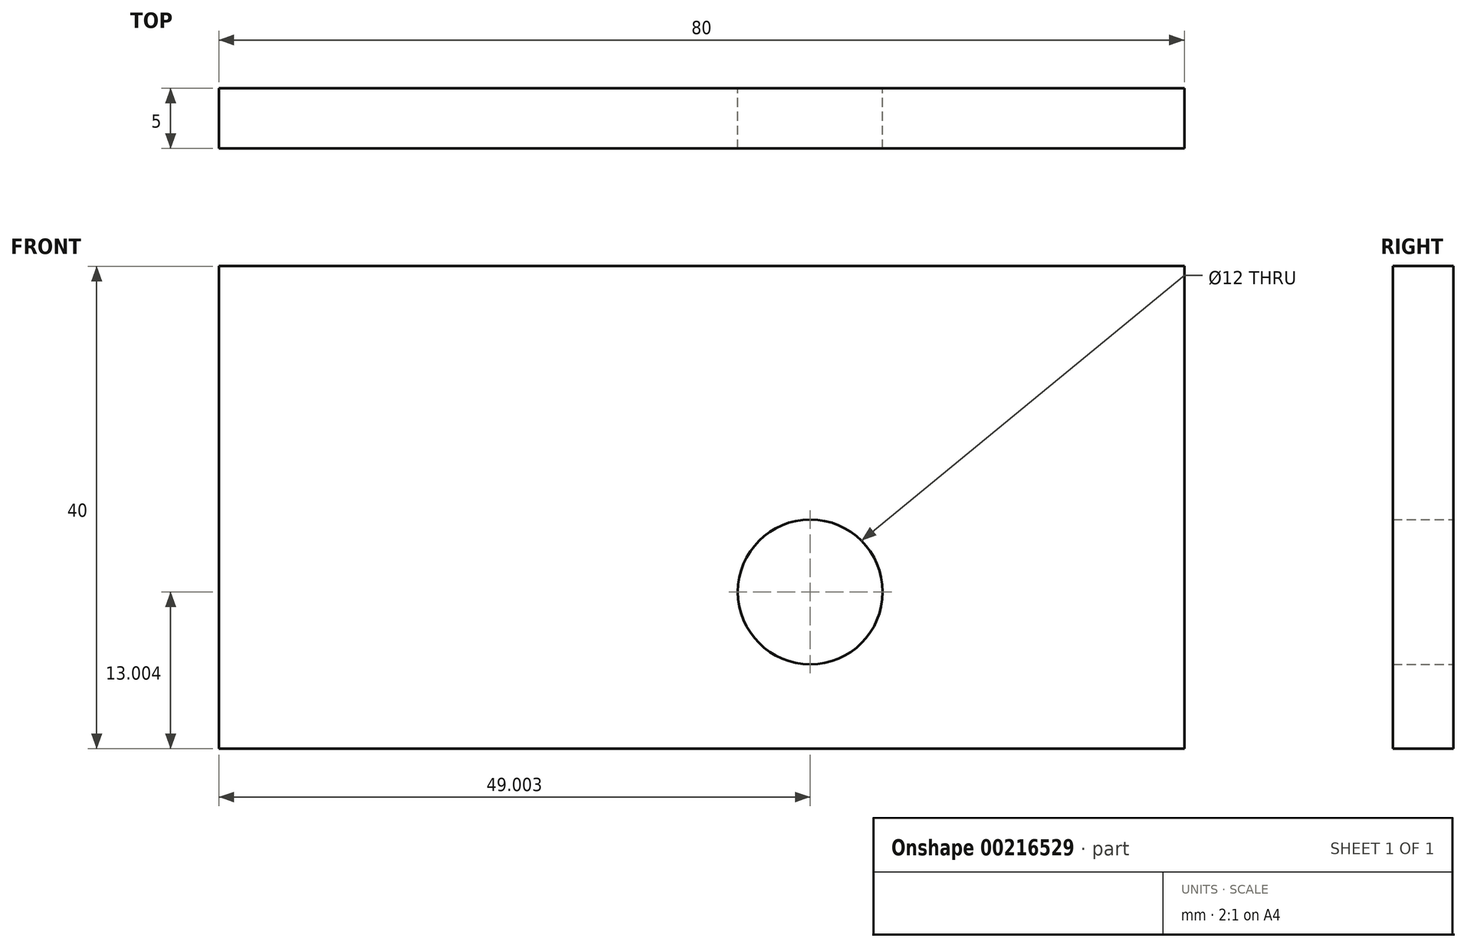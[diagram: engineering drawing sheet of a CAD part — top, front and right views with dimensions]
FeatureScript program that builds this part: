
annotation { "Feature Type Name" : "Feature", "Feature Type Description" : "" }
export const myFeature = defineFeature(function(context is Context, id is Id, definition is map)
    precondition{}
    {
        {
            var Q0;
            Q0=qCreatedBy(makeId("Front.planeOp"),FACE);
            var sketch = newSketch(context, id + "F0", { "sketchPlane" : qUnion([Q0])});
            skLineSegment(sketch, "E0.bottom", {"start": v(-38.89, 16.98) * mm, "end": v(41.11, 16.98) * mm});
            skLineSegment(sketch, "E0.top", {"start": v(-38.89, -23.02) * mm, "end": v(41.11, -23.02) * mm});
            skLineSegment(sketch, "E0.left", {"start": v(-38.89, 16.98) * mm, "end": v(-38.89, -23.02) * mm});
            skLineSegment(sketch, "E0.right", {"start": v(41.11, 16.98) * mm, "end": v(41.11, -23.02) * mm});
            skCircle(sketch, "E1", {"center": v(10.11, -10.02) * mm, "radius": 6 * mm});
            skSolve(sketch);
        }
        {
            var Q0;
            Q0 = qSketchRegion(id + "F0", true);
            extrude(context, id + "F1", {"entities" : qUnion([Q0]), "depth" : 5 * mm});
        }
    });
